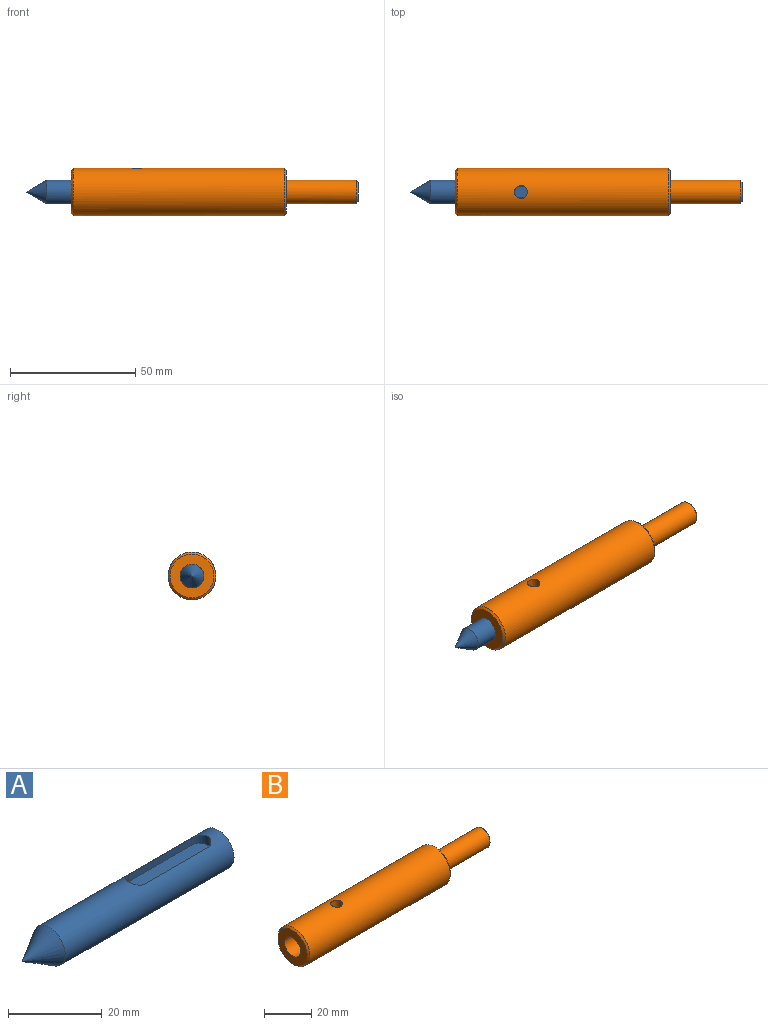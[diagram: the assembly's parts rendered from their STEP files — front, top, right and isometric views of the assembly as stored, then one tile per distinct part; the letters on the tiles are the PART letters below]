
ASSEMBLY  parts=2 mates=1
PART A: 8 faces, bbox 59x9.5x9.5 mm
  f0: cylinder r=4.76mm len=50.8mm, axis (-1,0,0), area 1406.7mm2, adj f1,f2,f3,f4,f5,f6
  f1: plane 9.53x9.53mm, normal (1,0,0), area 71.3mm2, adj f0
  f2: cone r=4.76mm half-angle=30deg, axis (1,0,0), area 142.5mm2, adj f0
  f3: cylinder r=2.38mm len=4.76mm, axis (0,0,1), area 15.5mm2, adj f0,f4,f6,f7
  f4: plane 19.05x1.74mm, normal (0,1,0), area 33.2mm2, adj f0,f3,f5,f7
  f5: cylinder r=2.38mm len=4.76mm, axis (0,0,1), area 15.5mm2, adj f0,f4,f6,f7
  f6: plane 19.05x1.74mm, normal (0,-1,0), area 33.2mm2, adj f0,f3,f5,f7
  f7: plane 23.81x4.76mm, normal (0,0,1), area 108.5mm2, adj f3,f4,f5,f6
PART B: 11 faces, bbox 114.3x19.1x19.1 mm
  f0: cylinder r=4.76mm len=76.2mm, axis (-1,0,0), area 2258.9mm2, adj f2,f6,f10
  f1: cylinder r=9.53mm len=84.14mm, axis (-1,0,0), area 5014.8mm2, adj f8,f9,f10
  f2: plane 9.53x9.53mm, normal (-1,0,0), area 71.3mm2, adj f0
  f3: plane 7.94x7.94mm, normal (1,0,0), area 49.5mm2, adj f7
  f4: cylinder r=4.76mm len=27.78mm, axis (-1,0,0), area 831.3mm2, adj f5,f7
  f5: plane 17.46x17.46mm, normal (1,0,0), area 168.2mm2, adj f4,f8
  f6: plane 17.46x17.46mm, normal (-1,0,0), area 168.2mm2, adj f0,f9
  f7: cone r=4.76mm half-angle=45deg, axis (-1,0,0), area 30.8mm2, adj f3,f4
  f8: cone r=9.53mm half-angle=45deg, axis (-1,0,0), area 64.4mm2, adj f1,f5
  f9: cone r=8.73mm half-angle=45deg, axis (1,0,0), area 64.4mm2, adj f1,f6
  f10: cylinder r=2.55mm len=5.5mm, axis (0,0,1), area 79.4mm2, adj f0,f1
PLACE A rot(axis=(1,0,0),0deg) t=(29,12.01,15.65)mm
PLACE B rot(axis=(1,0,0),0deg) t=(19.75,12.01,15.65)mm
MATE slider A.f0 <-> B.f0  axis (-1,0,0) through (9.95,12.01,15.65)mm
